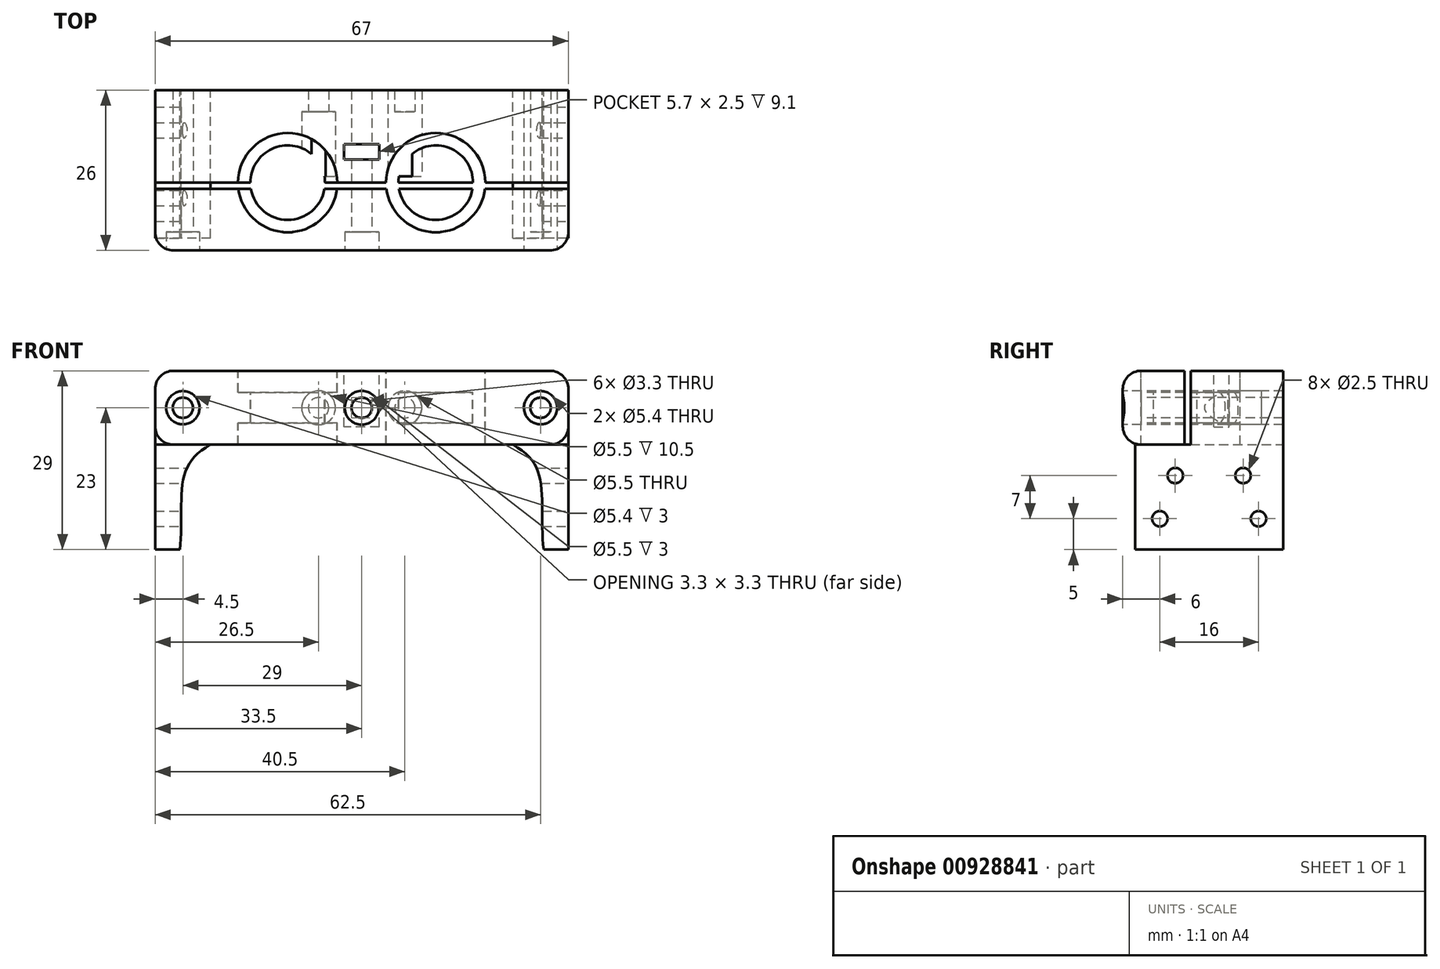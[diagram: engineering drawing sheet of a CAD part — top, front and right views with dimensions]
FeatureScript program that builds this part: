
annotation { "Feature Type Name" : "Feature", "Feature Type Description" : "" }
export const myFeature = defineFeature(function(context is Context, id is Id, definition is map)
    precondition{}
    {
        {
            var Q0;
            Q0=qCreatedBy(makeId("Front.planeOp"),FACE);
            var sketch = newSketch(context, id + "F0", { "sketchPlane" : qUnion([Q0])});
            skLineSegment(sketch, "E0.bottom", {"start": v(33.5, -6) * mm, "end": v(-33.5, -6) * mm});
            skLineSegment(sketch, "E0.top", {"start": v(33.5, 6) * mm, "end": v(-33.5, 6) * mm});
            skLineSegment(sketch, "E0.left", {"start": v(33.5, -6) * mm, "end": v(33.5, 6) * mm});
            skLineSegment(sketch, "E0.right", {"start": v(-33.5, -6) * mm, "end": v(-33.5, 6) * mm});
            skPoint(sketch, "E0.middle", {"position": v(0, 0) * mm});
            skLineSegment(sketch, "E1", {"start": v(-33.5, -23) * mm, "end": v(-33.5, -6) * mm});
            skLineSegment(sketch, "E2.MirrorCS", {"start": v(33.5, -23) * mm, "end": v(33.5, -6) * mm});
            skLineSegment(sketch, "E3", {"start": v(-33.5, -23) * mm, "end": v(-29.5, -23) * mm});
            skLineSegment(sketch, "E4.MirrorCS", {"start": v(33.5, -23) * mm, "end": v(29.5, -23) * mm});
            skFitSpline(sketch, "E5", {"points": [v(-24.5, -6) * mm, v(-29, -12) * mm, v(-29.5, -23) * mm], "startDerivative": vector(-19.18, -10.42) * mm, "endDerivative": vector(-2.52, -19.68) * mm});
            skFitSpline(sketch, "E6.MirrorCS", {"points": [v(24.5, -6) * mm, v(29, -12) * mm, v(29.5, -23) * mm], "startDerivative": vector(19.18, -10.42) * mm, "endDerivative": vector(2.52, -19.68) * mm});
            skSolve(sketch);
        }
        {
            var Q0;
            Q0=makeQuery(id+"F0.imprint","IMPRINT",FACE,{"disambiguationData":[TD([[makeQuery(id+"F0.imprint","IMPRINT",EDGE,{"derivedFrom":sQuery(id+"F0.wireOp",EDGE,"E0.top")}),1.0]])]});
            extrude(context, id + "F1", {"entities" : qUnion([Q0]), "depth" : 15 * mm, "offsetDistance" : 25 * mm});
        }
        {
            var Q0;
            {var subQ0=sQuery(id+"F0.wireOp",EDGE,"E1");Q0=makeQuery(id+"F0.imprint","IMPRINT",FACE,{"disambiguationData":[TD([[makeQuery(id+"F0.imprint","IMPRINT",EDGE,{"derivedFrom":subQ0}),-1.0]])]});}
            var Q1;
            {var subQ0=sQuery(id+"F0.wireOp",EDGE,"E2.MirrorCS");Q1=makeQuery(id+"F0.imprint","IMPRINT",FACE,{"disambiguationData":[TD([[makeQuery(id+"F0.imprint","IMPRINT",EDGE,{"derivedFrom":subQ0}),1.0]])]});}
            extrude(context, id + "F2", {"entities" : qUnion([Q0, Q1]), "operationType" : NewBodyOperationType.ADD, "depth" : 24 * mm, "offsetDistance" : 25 * mm});
        }
        {
            var Q0;
            Q0=makeQuery(id+"F1.opExtrude","SWEPT_FACE",FACE,{"disambiguationData":[OSD([sQuery(id+"F0.wireOp",EDGE,"E0.top")])]});
            var sketch = newSketch(context, id + "F3", { "sketchPlane" : qUnion([Q0])});
            skLineSegment(sketch, "E7", {"start": v(-33.5, -7) * mm, "end": v(33.5, -7) * mm, "construction": true});
            skLineSegment(sketch, "E8.bottom", {"start": v(2.85, -11.25) * mm, "end": v(-2.85, -11.25) * mm});
            skLineSegment(sketch, "E8.top", {"start": v(2.85, -8.75) * mm, "end": v(-2.85, -8.75) * mm});
            skLineSegment(sketch, "E8.left", {"start": v(2.85, -11.25) * mm, "end": v(2.85, -8.75) * mm});
            skLineSegment(sketch, "E8.right", {"start": v(-2.85, -11.25) * mm, "end": v(-2.85, -8.75) * mm});
            skPoint(sketch, "E8.middle", {"position": v(0, -10) * mm});
            skSolve(sketch);
        }
        {
            var Q0;
            Q0=makeQuery(id+"F3.imprint","IMPRINT",FACE,{"disambiguationData":[TD([[makeQuery(id+"F3.imprint","IMPRINT",EDGE,{"derivedFrom":sQuery(id+"F3.wireOp",EDGE,"jUf4XIvJ-XALh-Ccey-Qydy-tmJyOFJsBozL.bottom")}),-1.0]])]});
            var Q1;
            Q1=makeQuery(id+"F3.imprint","IMPRINT",FACE,{"disambiguationData":[TD([[makeQuery(id+"F3.imprint","IMPRINT",EDGE,{"derivedFrom":sQuery(id+"F3.wireOp",EDGE,"E8.bottom")}),-1.0]])]});
            var Q2;
            Q2=makeQuery(id+"F3.imprint","IMPRINT",FACE,{"disambiguationData":[TD([[makeQuery(id+"F3.imprint","IMPRINT",EDGE,{"derivedFrom":sQuery(id+"F3.wireOp",EDGE,"7975c7f9-c37b-4ea5-b004-56becf66a4950.MirrorCS")}),1.0]])]});
            extrude(context, id + "F4", {"entities" : qUnion([Q0, Q1, Q2]), "operationType" : NewBodyOperationType.REMOVE, "oppositeDirection" : true, "depth" : 9.1 * mm, "offsetDistance" : 25 * mm});
        }
        {
            var Q0;
            Q0=qCreatedBy(makeId("Top.planeOp"),FACE);
            var sketch = newSketch(context, id + "F5", { "sketchPlane" : qUnion([Q0])});
            skLineSegment(sketch, "E9.bottom", {"start": v(33.5, -26) * mm, "end": v(-33.5, -26) * mm});
            skLineSegment(sketch, "E9.top", {"start": v(33.5, -16) * mm, "end": v(-33.5, -16) * mm});
            skLineSegment(sketch, "E9.left", {"start": v(33.5, -26) * mm, "end": v(33.5, -16) * mm});
            skLineSegment(sketch, "E9.right", {"start": v(-33.5, -26) * mm, "end": v(-33.5, -16) * mm});
            skPoint(sketch, "E9.middle", {"position": v(0, -21) * mm});
            skSolve(sketch);
        }
        {
            var Q0;
            Q0=makeQuery(id+"F5.imprint","IMPRINT",FACE,{"disambiguationData":[TD([[makeQuery(id+"F5.imprint","IMPRINT",EDGE,{"derivedFrom":sQuery(id+"F5.wireOp",EDGE,"E9.bottom")}),-1.0]])]});
            extrude(context, id + "F6", {"entities" : qUnion([Q0]), "endBound" : BoundingType.SYMMETRIC, "depth" : 12 * mm, "offsetDistance" : 25 * mm});
        }
        {
            var Q0;
            Q0=makeQuery(id+"F6.opExtrude","SWEPT_FACE",FACE,{"disambiguationData":[OSD([sQuery(id+"F5.wireOp",EDGE,"E9.bottom")])]});
            var sketch = newSketch(context, id + "F7", { "sketchPlane" : qUnion([Q0])});
            skCircle(sketch, "E10", {"center": v(-7, 0) * mm, "radius": 1.65 * mm});
            skCircle(sketch, "E11.MirrorC", {"center": v(7, 0) * mm, "radius": 1.65 * mm});
            skCircle(sketch, "E12", {"center": v(-7, 0) * mm, "radius": 2.75 * mm});
            skCircle(sketch, "E13.MirrorC", {"center": v(7, 0) * mm, "radius": 2.75 * mm});
            skCircle(sketch, "E14", {"center": v(-29, 0) * mm, "radius": 1.65 * mm});
            skCircle(sketch, "E15", {"center": v(0, 0) * mm, "radius": 1.65 * mm});
            skCircle(sketch, "E16.MirrorC", {"center": v(29, 0) * mm, "radius": 1.65 * mm});
            skCircle(sketch, "E17", {"center": v(-29, 0) * mm, "radius": 2.7 * mm});
            skCircle(sketch, "E18", {"center": v(0, 0) * mm, "radius": 2.75 * mm});
            skCircle(sketch, "E19", {"center": v(29, 0) * mm, "radius": 2.7 * mm});
            skSolve(sketch);
        }
        {
            var Q0;
            Q0=makeQuery(id+"F7.imprint","IMPRINT",FACE,{"disambiguationData":[TD([[makeQuery(id+"F7.imprint","IMPRINT",EDGE,{"derivedFrom":sQuery(id+"F7.wireOp",EDGE,"E10")}),1.0]])]});
            var Q1;
            Q1=makeQuery(id+"F7.imprint","IMPRINT",FACE,{"disambiguationData":[TD([[makeQuery(id+"F7.imprint","IMPRINT",EDGE,{"derivedFrom":sQuery(id+"F7.wireOp",EDGE,"E11.MirrorC")}),-1.0]])]});
            extrude(context, id + "F8", {"entities" : qUnion([Q0, Q1]), "operationType" : NewBodyOperationType.REMOVE, "oppositeDirection" : true, "depth" : 30.5 * mm, "offsetDistance" : 25 * mm, "hasSecondDirection" : true, "secondDirectionOppositeDirection" : true, "secondDirectionDepth" : 12 * mm});
        }
        {
            var Q0;
            Q0=makeQuery(id+"F7.imprint","IMPRINT",FACE,{"disambiguationData":[TD([[makeQuery(id+"F7.imprint","IMPRINT",EDGE,{"derivedFrom":sQuery(id+"F7.wireOp",EDGE,"E10")}),-1.0]])]});
            var Q1;
            Q1=makeQuery(id+"F7.imprint","IMPRINT",FACE,{"disambiguationData":[TD([[makeQuery(id+"F7.imprint","IMPRINT",EDGE,{"derivedFrom":sQuery(id+"F7.wireOp",EDGE,"E11.MirrorC")}),1.0]])]});
            extrude(context, id + "F9", {"entities" : qUnion([Q0, Q1]), "operationType" : NewBodyOperationType.REMOVE, "oppositeDirection" : true, "depth" : 22.5 * mm, "offsetDistance" : 25 * mm, "hasSecondDirection" : true, "secondDirectionOppositeDirection" : true, "secondDirectionDepth" : 12 * mm});
        }
        {
            var Q0;
            Q0=makeQuery(id+"F7.imprint","IMPRINT",FACE,{"disambiguationData":[TD([[makeQuery(id+"F7.imprint","IMPRINT",EDGE,{"derivedFrom":sQuery(id+"F7.wireOp",EDGE,"E14")}),1.0]])]});
            var Q1;
            Q1=makeQuery(id+"F7.imprint","IMPRINT",FACE,{"disambiguationData":[TD([[makeQuery(id+"F7.imprint","IMPRINT",EDGE,{"derivedFrom":sQuery(id+"F7.wireOp",EDGE,"E15")}),1.0]])]});
            var Q2;
            Q2=makeQuery(id+"F7.imprint","IMPRINT",FACE,{"disambiguationData":[TD([[makeQuery(id+"F7.imprint","IMPRINT",EDGE,{"derivedFrom":sQuery(id+"F7.wireOp",EDGE,"E16.MirrorC")}),-1.0]])]});
            extrude(context, id + "F10", {"entities" : qUnion([Q0, Q1, Q2]), "operationType" : NewBodyOperationType.REMOVE, "oppositeDirection" : true, "depth" : 45 * mm, "offsetDistance" : 25 * mm});
        }
        {
            var Q0;
            Q0=makeQuery(id+"F1.opExtrude","SWEPT_FACE",FACE,{"disambiguationData":[OSD([sQuery(id+"F0.wireOp",EDGE,"E0.top")])]});
            var sketch = newSketch(context, id + "F11", { "sketchPlane" : qUnion([Q0])});
            skCircle(sketch, "E20", {"center": v(-12, -15) * mm, "radius": 8.05 * mm});
            skCircle(sketch, "E21", {"center": v(-12, -15) * mm, "radius": 6.05 * mm});
            skCircle(sketch, "E22.MirrorC", {"center": v(12, -15) * mm, "radius": 6.05 * mm});
            skCircle(sketch, "E23.MirrorC", {"center": v(12, -15) * mm, "radius": 8.05 * mm});
            skSolve(sketch);
        }
        {
            var Q0;
            {var subQ0=sQuery(id+"F11.wireOp",EDGE,"E21");var subQ1=makeQuery(id+"F1.opExtrude","CAP_EDGE",EDGE,{"disambiguationData":[OSD([sQuery(id+"F0.wireOp",EDGE,"E0.top")])],"isStart":false});var subQ2=makeQuery(id+"F11.imprint","INTERSECT",VERTEX,{"disambiguationData":[OD(0.0)],"derivedFrom":[subQ1,subQ0]});Q0=makeQuery(id+"F11.imprint","IMPRINT",FACE,{"disambiguationData":[TD([[makeQuery(id+"F11.imprint","IMPRINT",EDGE,{"disambiguationData":[TD([[subQ2,1.0]])],"derivedFrom":subQ0}),1.0]])]});}
            var Q1;
            {var subQ0=sQuery(id+"F11.wireOp",EDGE,"E22.MirrorC");var subQ1=makeQuery(id+"F1.opExtrude","CAP_EDGE",EDGE,{"disambiguationData":[OSD([sQuery(id+"F0.wireOp",EDGE,"E0.top")])],"isStart":false});var subQ2=makeQuery(id+"F11.imprint","INTERSECT",VERTEX,{"disambiguationData":[OD(0.0)],"derivedFrom":[subQ1,subQ0]});Q1=makeQuery(id+"F11.imprint","IMPRINT",FACE,{"disambiguationData":[TD([[makeQuery(id+"F11.imprint","IMPRINT",EDGE,{"disambiguationData":[TD([[subQ2,1.0]])],"derivedFrom":subQ0}),-1.0]])]});}
            var Q2;
            {var subQ0=sQuery(id+"F11.wireOp",EDGE,"E21");var subQ1=makeQuery(id+"F1.opExtrude","CAP_EDGE",EDGE,{"disambiguationData":[OSD([sQuery(id+"F0.wireOp",EDGE,"E0.top")])],"isStart":false});var subQ2=makeQuery(id+"F11.imprint","INTERSECT",VERTEX,{"disambiguationData":[OD(0.0)],"derivedFrom":[subQ1,subQ0]});Q2=makeQuery(id+"F11.imprint","IMPRINT",FACE,{"disambiguationData":[TD([[makeQuery(id+"F11.imprint","IMPRINT",EDGE,{"disambiguationData":[TD([[subQ2,-1.0]])],"derivedFrom":subQ0}),1.0]])]});}
            var Q3;
            {var subQ0=sQuery(id+"F11.wireOp",EDGE,"E22.MirrorC");var subQ1=makeQuery(id+"F1.opExtrude","CAP_EDGE",EDGE,{"disambiguationData":[OSD([sQuery(id+"F0.wireOp",EDGE,"E0.top")])],"isStart":false});var subQ2=makeQuery(id+"F11.imprint","INTERSECT",VERTEX,{"disambiguationData":[OD(0.0)],"derivedFrom":[subQ1,subQ0]});Q3=makeQuery(id+"F11.imprint","IMPRINT",FACE,{"disambiguationData":[TD([[makeQuery(id+"F11.imprint","IMPRINT",EDGE,{"disambiguationData":[TD([[subQ2,-1.0]])],"derivedFrom":subQ0}),-1.0]])]});}
            extrude(context, id + "F12", {"entities" : qUnion([Q0, Q1, Q2, Q3]), "operationType" : NewBodyOperationType.REMOVE, "endBound" : BoundingType.THROUGH_ALL, "oppositeDirection" : true, "depth" : 25 * mm, "offsetDistance" : 25 * mm});
        }
        {
            var Q0;
            {var subQ0=sQuery(id+"F11.wireOp",EDGE,"E20");var subQ1=makeQuery(id+"F1.opExtrude","CAP_EDGE",EDGE,{"disambiguationData":[OSD([sQuery(id+"F0.wireOp",EDGE,"E0.top")])],"isStart":false});var subQ2=makeQuery(id+"F11.imprint","INTERSECT",VERTEX,{"disambiguationData":[OD(0.0)],"derivedFrom":[subQ1,subQ0]});Q0=makeQuery(id+"F11.imprint","IMPRINT",FACE,{"disambiguationData":[TD([[makeQuery(id+"F11.imprint","IMPRINT",EDGE,{"disambiguationData":[TD([[subQ2,1.0]])],"derivedFrom":subQ0}),1.0]])]});}
            var Q1;
            {var subQ0=sQuery(id+"F11.wireOp",EDGE,"E22.MirrorC");var subQ1=makeQuery(id+"F1.opExtrude","CAP_EDGE",EDGE,{"disambiguationData":[OSD([sQuery(id+"F0.wireOp",EDGE,"E0.top")])],"isStart":false});var subQ2=makeQuery(id+"F11.imprint","INTERSECT",VERTEX,{"disambiguationData":[OD(0.0)],"derivedFrom":[subQ1,subQ0]});Q1=makeQuery(id+"F11.imprint","IMPRINT",FACE,{"disambiguationData":[TD([[makeQuery(id+"F11.imprint","IMPRINT",EDGE,{"disambiguationData":[TD([[subQ2,1.0]])],"derivedFrom":subQ0}),1.0]])]});}
            var Q2;
            {var subQ0=sQuery(id+"F11.wireOp",EDGE,"E20");var subQ1=makeQuery(id+"F1.opExtrude","CAP_EDGE",EDGE,{"disambiguationData":[OSD([sQuery(id+"F0.wireOp",EDGE,"E0.top")])],"isStart":false});var subQ2=makeQuery(id+"F11.imprint","INTERSECT",VERTEX,{"disambiguationData":[OD(0.0)],"derivedFrom":[subQ1,subQ0]});Q2=makeQuery(id+"F11.imprint","IMPRINT",FACE,{"disambiguationData":[TD([[makeQuery(id+"F11.imprint","IMPRINT",EDGE,{"disambiguationData":[TD([[subQ2,-1.0]])],"derivedFrom":subQ0}),1.0]])]});}
            var Q3;
            {var subQ0=sQuery(id+"F11.wireOp",EDGE,"E22.MirrorC");var subQ1=makeQuery(id+"F1.opExtrude","CAP_EDGE",EDGE,{"disambiguationData":[OSD([sQuery(id+"F0.wireOp",EDGE,"E0.top")])],"isStart":false});var subQ2=makeQuery(id+"F11.imprint","INTERSECT",VERTEX,{"disambiguationData":[OD(0.0)],"derivedFrom":[subQ1,subQ0]});Q3=makeQuery(id+"F11.imprint","IMPRINT",FACE,{"disambiguationData":[TD([[makeQuery(id+"F11.imprint","IMPRINT",EDGE,{"disambiguationData":[TD([[subQ2,-1.0]])],"derivedFrom":subQ0}),1.0]])]});}
            extrude(context, id + "F13", {"entities" : qUnion([Q0, Q1, Q2, Q3]), "operationType" : NewBodyOperationType.REMOVE, "oppositeDirection" : true, "depth" : 3.5 * mm, "offsetDistance" : 25 * mm});
        }
        {
            var Q0;
            {var subQ0=sQuery(id+"F11.wireOp",EDGE,"E20");var subQ1=makeQuery(id+"F1.opExtrude","CAP_EDGE",EDGE,{"disambiguationData":[OSD([sQuery(id+"F0.wireOp",EDGE,"E0.top")])],"isStart":false});var subQ2=makeQuery(id+"F11.imprint","INTERSECT",VERTEX,{"disambiguationData":[OD(0.0)],"derivedFrom":[subQ1,subQ0]});Q0=makeQuery(id+"F11.imprint","IMPRINT",FACE,{"disambiguationData":[TD([[makeQuery(id+"F11.imprint","IMPRINT",EDGE,{"disambiguationData":[TD([[subQ2,1.0]])],"derivedFrom":subQ0}),1.0]])]});}
            var Q1;
            {var subQ0=sQuery(id+"F11.wireOp",EDGE,"E22.MirrorC");var subQ1=makeQuery(id+"F1.opExtrude","CAP_EDGE",EDGE,{"disambiguationData":[OSD([sQuery(id+"F0.wireOp",EDGE,"E0.top")])],"isStart":false});var subQ2=makeQuery(id+"F11.imprint","INTERSECT",VERTEX,{"disambiguationData":[OD(0.0)],"derivedFrom":[subQ1,subQ0]});Q1=makeQuery(id+"F11.imprint","IMPRINT",FACE,{"disambiguationData":[TD([[makeQuery(id+"F11.imprint","IMPRINT",EDGE,{"disambiguationData":[TD([[subQ2,1.0]])],"derivedFrom":subQ0}),1.0]])]});}
            var Q2;
            {var subQ0=sQuery(id+"F11.wireOp",EDGE,"E20");var subQ1=makeQuery(id+"F1.opExtrude","CAP_EDGE",EDGE,{"disambiguationData":[OSD([sQuery(id+"F0.wireOp",EDGE,"E0.top")])],"isStart":false});var subQ2=makeQuery(id+"F11.imprint","INTERSECT",VERTEX,{"disambiguationData":[OD(0.0)],"derivedFrom":[subQ1,subQ0]});Q2=makeQuery(id+"F11.imprint","IMPRINT",FACE,{"disambiguationData":[TD([[makeQuery(id+"F11.imprint","IMPRINT",EDGE,{"disambiguationData":[TD([[subQ2,-1.0]])],"derivedFrom":subQ0}),1.0]])]});}
            var Q3;
            {var subQ0=sQuery(id+"F11.wireOp",EDGE,"E22.MirrorC");var subQ1=makeQuery(id+"F1.opExtrude","CAP_EDGE",EDGE,{"disambiguationData":[OSD([sQuery(id+"F0.wireOp",EDGE,"E0.top")])],"isStart":false});var subQ2=makeQuery(id+"F11.imprint","INTERSECT",VERTEX,{"disambiguationData":[OD(0.0)],"derivedFrom":[subQ1,subQ0]});Q3=makeQuery(id+"F11.imprint","IMPRINT",FACE,{"disambiguationData":[TD([[makeQuery(id+"F11.imprint","IMPRINT",EDGE,{"disambiguationData":[TD([[subQ2,-1.0]])],"derivedFrom":subQ0}),1.0]])]});}
            extrude(context, id + "F14", {"entities" : qUnion([Q0, Q1, Q2, Q3]), "operationType" : NewBodyOperationType.REMOVE, "oppositeDirection" : true, "depth" : 12 * mm, "offsetDistance" : 25 * mm, "hasSecondDirection" : true, "secondDirectionOppositeDirection" : true, "secondDirectionDepth" : 8.5 * mm});
        }
        {
            var Q0;
            Q0=makeQuery(id+"F7.imprint","IMPRINT",FACE,{"disambiguationData":[TD([[makeQuery(id+"F7.imprint","IMPRINT",EDGE,{"derivedFrom":sQuery(id+"F7.wireOp",EDGE,"E14")}),-1.0]])]});
            var Q1;
            Q1=makeQuery(id+"F7.imprint","IMPRINT",FACE,{"disambiguationData":[TD([[makeQuery(id+"F7.imprint","IMPRINT",EDGE,{"derivedFrom":sQuery(id+"F7.wireOp",EDGE,"E16.MirrorC")}),1.0]])]});
            var Q2;
            Q2=makeQuery(id+"F7.imprint","IMPRINT",FACE,{"disambiguationData":[TD([[makeQuery(id+"F7.imprint","IMPRINT",EDGE,{"derivedFrom":sQuery(id+"F7.wireOp",EDGE,"E15")}),-1.0]])]});
            extrude(context, id + "F15", {"entities" : qUnion([Q0, Q1, Q2]), "operationType" : NewBodyOperationType.REMOVE, "oppositeDirection" : true, "depth" : 3 * mm, "offsetDistance" : 25 * mm});
        }
        {
            var Q0;
            Q0=makeQuery(id+"F1.opExtrude","SWEPT_EDGE",EDGE,{"disambiguationData":[OSD([sQuery(id+"F0.wireOp",EDGE,"E0.top"),sQuery(id+"F0.wireOp",EDGE,"E0.left")])]});
            var Q1;
            Q1=makeQuery(id+"F6.opExtrude","SWEPT_EDGE",EDGE,{"disambiguationData":[OSD([sQuery(id+"F5.wireOp",EDGE,"E9.bottom"),sQuery(id+"F5.wireOp",EDGE,"E9.right")])]});
            var Q2;
            Q2=makeQuery(id+"F6.opExtrude","SWEPT_EDGE",EDGE,{"disambiguationData":[OSD([sQuery(id+"F5.wireOp",EDGE,"E9.bottom"),sQuery(id+"F5.wireOp",EDGE,"E9.left")])]});
            var Q3;
            Q3=makeQuery(id+"F6.opExtrude","CAP_EDGE",EDGE,{"disambiguationData":[OSD([sQuery(id+"F5.wireOp",EDGE,"E9.bottom")])],"isStart":false});
            var Q4;
            Q4=makeQuery(id+"F6.opExtrude","CAP_EDGE",EDGE,{"disambiguationData":[OSD([sQuery(id+"F5.wireOp",EDGE,"E9.right")])],"isStart":false});
            var Q5;
            Q5=makeQuery(id+"F6.opExtrude","CAP_EDGE",EDGE,{"disambiguationData":[OSD([sQuery(id+"F5.wireOp",EDGE,"E9.left")])],"isStart":true});
            var Q6;
            Q6=makeQuery(id+"F6.opExtrude","CAP_EDGE",EDGE,{"disambiguationData":[OSD([sQuery(id+"F5.wireOp",EDGE,"E9.left")])],"isStart":false});
            var Q7;
            Q7=makeQuery(id+"F6.opExtrude","CAP_EDGE",EDGE,{"disambiguationData":[OSD([sQuery(id+"F5.wireOp",EDGE,"E9.right")])],"isStart":true});
            var Q8;
            Q8=makeQuery(id+"F6.opExtrude","CAP_EDGE",EDGE,{"disambiguationData":[OSD([sQuery(id+"F5.wireOp",EDGE,"E9.bottom")])],"isStart":true});
            var Q9;
            Q9=makeQuery(id+"F1.opExtrude","SWEPT_EDGE",EDGE,{"disambiguationData":[OSD([sQuery(id+"F0.wireOp",EDGE,"E0.top"),sQuery(id+"F0.wireOp",EDGE,"E0.right")])]});
            var Q10;
            Q10=makeQuery(id+"F1.opExtrude","SWEPT_EDGE",EDGE,{"disambiguationData":[OSD([sQuery(id+"F0.wireOp",EDGE,"E2.MirrorCS"),sQuery(id+"F0.wireOp",EDGE,"E4.MirrorCS")])]});
            var Q11;
            Q11=makeQuery(id+"F1.opExtrude","SWEPT_EDGE",EDGE,{"disambiguationData":[OSD([sQuery(id+"F0.wireOp",EDGE,"E1"),sQuery(id+"F0.wireOp",EDGE,"E3")])]});
            fillet(context, id + "F16", {"entities" : qUnion([Q0, Q1, Q2, Q3, Q4, Q5, Q6, Q7, Q8, Q9, Q10, Q11]), "radius" : 3 * mm, "tangentPropagation" : true, "allowEdgeOverflow" : false});
        }
        {
            var Q0;
            Q0=makeQuery(id+"F2.boolean.opBoolean","MERGE",FACE,{"derivedFrom":[makeQuery(id+"F1.opExtrude","SWEPT_FACE",FACE,{"disambiguationData":[OSD([sQuery(id+"F0.wireOp",EDGE,"E0.left")])]}),makeQuery(id+"F2.opExtrude","SWEPT_FACE",FACE,{"disambiguationData":[OSD([sQuery(id+"F0.wireOp",EDGE,"E2.MirrorCS")])]})]});
            var sketch = newSketch(context, id + "F17", { "sketchPlane" : qUnion([Q0])});
            skLineSegment(sketch, "E24", {"start": v(-24, -14.5) * mm, "end": v(0, -14.5) * mm, "construction": true});
            skLineSegment(sketch, "E25", {"start": v(-12, -23) * mm, "end": v(-12, 3) * mm, "construction": true});
            skCircle(sketch, "E26", {"center": v(-17.5, -11) * mm, "radius": 1.25 * mm});
            skCircle(sketch, "E27.MirrorC", {"center": v(-6.5, -11) * mm, "radius": 1.25 * mm});
            skCircle(sketch, "E28", {"center": v(-20, -18) * mm, "radius": 1.25 * mm});
            skCircle(sketch, "E29.MirrorC", {"center": v(-4, -18) * mm, "radius": 1.25 * mm});
            skSolve(sketch);
        }
        {
            var Q0;
            Q0=qSketchRegion(id+"F17",true);
            extrude(context, id + "F18", {"entities" : qUnion([Q0]), "operationType" : NewBodyOperationType.REMOVE, "oppositeDirection" : true, "depth" : 100 * mm, "offsetDistance" : 25 * mm});
        }
    });
